# Revit family: Door closer BTS80_Single Access_Double Door
name_source: partatom
category: Türen
revit_build: Autodesk Revit 2016 (Build: 20150220_1215(x64)
units: mm (PartAtom-declared; Revit-internal decimal feet)

## family parameters
Basisbauteil = Wand
Beim Laden mit Abzugskörper schneiden = Nein
Gemeinsam genutzt = Nein
Immer vertikal = Ja
OmniClass-Nummer = 23.30.10.00
OmniClass-Titel = Doors
Raumberechnungspunkt = Nein

## types (1)
- Door closer BTS80_Single Access_Double Door
    Depth (mm) = 78
    Design country = Germany
    Edition number = 1
    Glass material = Glass
    Height (mm) = 60
    Hersteller = DORMA
    IFC Classification = Door
    Installation instructions = http://www.dorma.de
    Manufacturer country = Germany
    Material main = Stainless steel
    Material secondary = Metal
    Panel material = Aluminum
    Product data url = http://www.dorma.de
    Product family = Door Control
    Product group = Door Hardware
    UNSPC Name = Elkraftsutrustning och tillbehör
    UNSPC code = 26
    Wandabschluss = Nach Basisbauteil
    Weight Net (Kg) = 0
    Width (mm) = 341

## geometry (parser evidence)
native form markers: Blend x4, Sweep x13
no freeform markers — native parametric forms only
